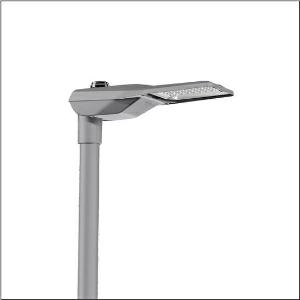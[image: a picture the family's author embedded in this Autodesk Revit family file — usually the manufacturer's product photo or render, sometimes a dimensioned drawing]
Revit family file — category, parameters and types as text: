
# Revit family: streetlight_sl_21_mini___st1_0a_5xe6d47n08jb_8270
name_source: partatom
category: Lighting Fixtures
units: mm (PartAtom-declared; Revit-internal decimal feet)

## family parameters
Cut with Voids When Loaded = No
Host = Face
Light Source = No
Part Type = Normal
Room Calculation Point = No
Round Connector Dimension = Use Diameter
Shared = No

## types (1)
- --- (1 x LED, 13390 lm, 87.3 W, 4000K)
    Apparent Load = 87 VA
    CIE Flux Codes = 40 73 97 100 100
    Color Rendering = 70
    Color Temperature = 4000K
    Default Elevation = 1800 mm
    Description = Streetlight SL 21 mini, mast luminaire, primary light control with lens, of PMMA, primary optical cover: cover, of toughened safety glass, transparent, light distribution: ST1.0a, light emission: direct distribution, primary light characteristic: asymmetric, installation type: side-entry, LED, 3G 2.5mm², High Power LED, rated luminous flux: 13.390lm, luminous efficacy: 153lm/W, light colour: 740, colour temperature: 4000K, control: overheat protection, pre-setting: linear dimming characteristic, constant luminous flux control, time-dependent luminous flux control, flexible luminous flux parameterisation, mains connection: 230..240V, AC, 50/60Hz, connection cable pre-assembled, cable length: 10,5m, wiring characteristics: H05VV-F, start of lifetime: 87W, end of service life: 90W, reduction: 40W, luminaire housing, of diecast aluminium (EN AC-44300), powder-coated, Siteco® metallic grey (DB 702S), corrosivity category C5 mid according to DIN EN ISO 12944, multi-level sealing system, sealing non-destructively replaceable, inclination adjustable: 0°, 5°, 10°, 15°, length: 628mm, width: 235mm, height: 110mm, spigot size: 42mm (side-entry), protection rating (complete): IP66, insulation class (complete): insulation class I (protective earthing), certification: CE, ENEC, ENEC+, VDE, impact resistance: IK09, permissible operating ambient temperature for outdoor applications: -40..+50°C, standard-compliant lighting for roads and squares, packaging unit: 1 piece

Light Distribution: ST1.0a
    Height = 110 mm
    Lamp = 1 x LED
    Lamp Light Flux = 13390 lm
    Lamp Power = 87.3 W
    Lamp count = 1
    Length = 625 mm
    Luminous efficacy = 153 lm/W
    Manufacturer = Siteco
    ModVariant = No
    Model = 5XE6D47N08JB
    Number of Poles = 1
    OnlyDefault = Yes
    Power Factor = 1
    Product Name = Streetlight SL 21 mini | ST1.0a
    Product group = mast luminaire | pylon top
    ProductGroupID = 6100
    Protection Class = Protection class I
    Protection Degree = IP 66
    RLX_Detail_Level = 1
    RLX_Emergency_Light_Flux = 0 lm
    RLX_Emergency_Type = 0
    RLX_Emergency_Type_DB = No
    RlxData = <blob elided: 92133 chars, md5=11d1996d>
    Socket = socket
    Standby Power = 0 W
    System Light Flux = 13390 lm
    System Power = 87 W
    Type Comments = factory setting: luminous flux: 100 % | dim-lin: 254 | 915 mA
    Type Image = l_1294379.jpg
    URL = http://relux.com
    VarID = @adj_105125
    Voltage = 0 V
    Weight = 0.00 kg
    Width = 234 mm

## geometry (parser evidence)
native form markers: Blend x4, Sweep x10
no freeform markers — native parametric forms only
